# Revit family: P500313-175
name_source: partatom
category: Lighting Fixtures
revit_build: Autodesk Revit 2014 (Build: 20130308_1515(x64)
units: mm (PartAtom-declared; Revit-internal decimal feet)

## types (1)
- P500313-175
    Apparent Load = 75 VA
    Assembly Code = D5020200
    Color Filter = 16777215
    Connector Description = Lighting Connector
    Default Elevation = 48 "
    Description = Terrazzo Collection One-Light Distressed Brass and Sand Terrazzo Hanging Pendant Light
    Dimming Lamp Color Temperature Shift = <None>
    Fab = Fabric
    Features = Application: Express an artistic sensibility with the Terrazzo Collection 1-Light Distressed Brass/Sandstone Concrete Terrazzo Global Hanging Pendant Light ideal for any foyer, dining room, kitchen, breakfast nook, entryway, living room, or stairway.
Styles: Perfect for global, urban industrial, and transitional style settings.
Finish: A polished sandstone concrete composite shade flecked with warm earthy hues offers a sophisticated contrast to its round distressed brass accent plate and stem suspension.
Materials: Constructed from steel to ensure a long product lifespan.
Glass/Shades: The light fixture creates beautifully focused task lighting.
Bulbs: For ideal illumination, use 1 medium base bulb that is sold separately (75w max - LED/CFL/incandescent). Compatible with dimmable bulbs.
Dimensions: Measures 10-inch diameter by 9-3/8-inch height.
Certifications: cULus damp location listed.
Pairs With: Pairs with the Hedgerow and Bonn collections from Progress Lighting.
Warranty: Our 1-Year Limited Warranty guarantees your complete satisfaction with your purchase and includes professional after-sales customer service support.
    Fixture distribution = Direct
    Glass = Paint - Hubbell - White Texture
    Gold = Hubbell - Gold
    Housing Material = Hubbell Metal Brass
    Lamp = LED/CFL/incandescent
    Load Classification = Lighting
    Manufacturer = Progress Lighting
    Model = P500313-175
    Photometric Web File = generic
    Power Factor = 1
    Product Documentation Link = https://hubbellcdn.com
    Product Link = https://www.hubbell.com
    Support = Paint - Hubbell - Light Silver
    Tilt Angle = 60.00°
    URL = https://www.hubbell.com
    Voltage = 120 V
    Warranty = 1 year Warranty
    Wattage Comments = 75W
    Watts = 75 W

## geometry (parser evidence)
native form markers: Sweep x5
no freeform markers — native parametric forms only
